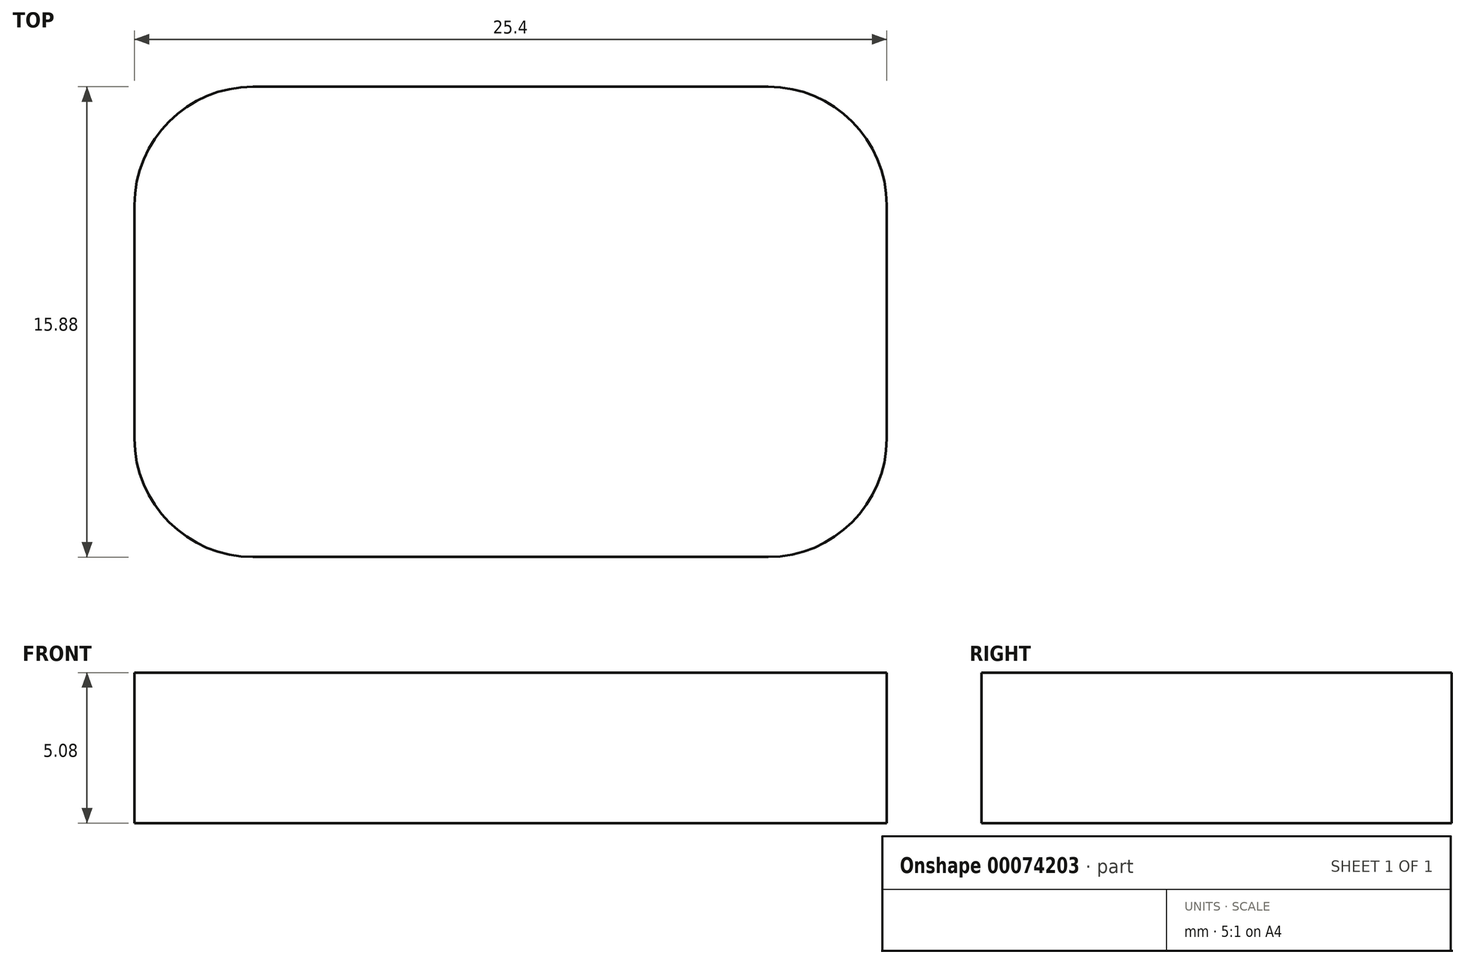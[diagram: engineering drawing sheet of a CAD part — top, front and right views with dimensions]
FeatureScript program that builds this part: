
annotation { "Feature Type Name" : "Feature", "Feature Type Description" : "" }
export const myFeature = defineFeature(function(context is Context, id is Id, definition is map)
    precondition{}
    {
        {
            var Q0;
            Q0=qCreatedBy(makeId("Top.planeOp"),FACE);
            var sketch = newSketch(context, id + "F0", { "sketchPlane" : qUnion([Q0])});
            skLineSegment(sketch, "E0.bottom", {"start": v(12.7, 7.94) * mm, "end": v(-12.7, 7.94) * mm});
            skLineSegment(sketch, "E0.top", {"start": v(12.7, -7.94) * mm, "end": v(-12.7, -7.94) * mm});
            skLineSegment(sketch, "E0.left", {"start": v(12.7, 7.94) * mm, "end": v(12.7, -7.94) * mm});
            skLineSegment(sketch, "E0.right", {"start": v(-12.7, 7.94) * mm, "end": v(-12.7, -7.94) * mm});
            skPoint(sketch, "E0.middle", {"position": v(0, 0) * mm});
            skSolve(sketch);
        }
        {
            var Q0;
            Q0 = qSketchRegion(id + "F0", true);
            extrude(context, id + "F1", {"entities" : qUnion([Q0]), "depth" : 5.08 * mm});
        }
        {
            var Q0;
            Q0=makeQuery(id+"F1.opExtrude","SWEPT_EDGE",EDGE,{"disambiguationData":[OSD([sQuery(id+"F0.wireOp",EDGE,"E0.top"),sQuery(id+"F0.wireOp",EDGE,"E0.right")])]});
            var Q1;
            Q1=makeQuery(id+"F1.opExtrude","SWEPT_EDGE",EDGE,{"disambiguationData":[OSD([sQuery(id+"F0.wireOp",EDGE,"E0.bottom"),sQuery(id+"F0.wireOp",EDGE,"E0.right")])]});
            var Q2;
            Q2=makeQuery(id+"F1.opExtrude","SWEPT_EDGE",EDGE,{"disambiguationData":[OSD([sQuery(id+"F0.wireOp",EDGE,"E0.bottom"),sQuery(id+"F0.wireOp",EDGE,"E0.left")])]});
            var Q3;
            Q3=makeQuery(id+"F1.opExtrude","SWEPT_EDGE",EDGE,{"disambiguationData":[OSD([sQuery(id+"F0.wireOp",EDGE,"E0.top"),sQuery(id+"F0.wireOp",EDGE,"E0.left")])]});
            fillet(context, id + "F2", {"entities" : qUnion([Q0, Q1, Q2, Q3]), "radius" : 4 * mm, "tangentPropagation" : true, "allowEdgeOverflow" : false});
        }
    });
